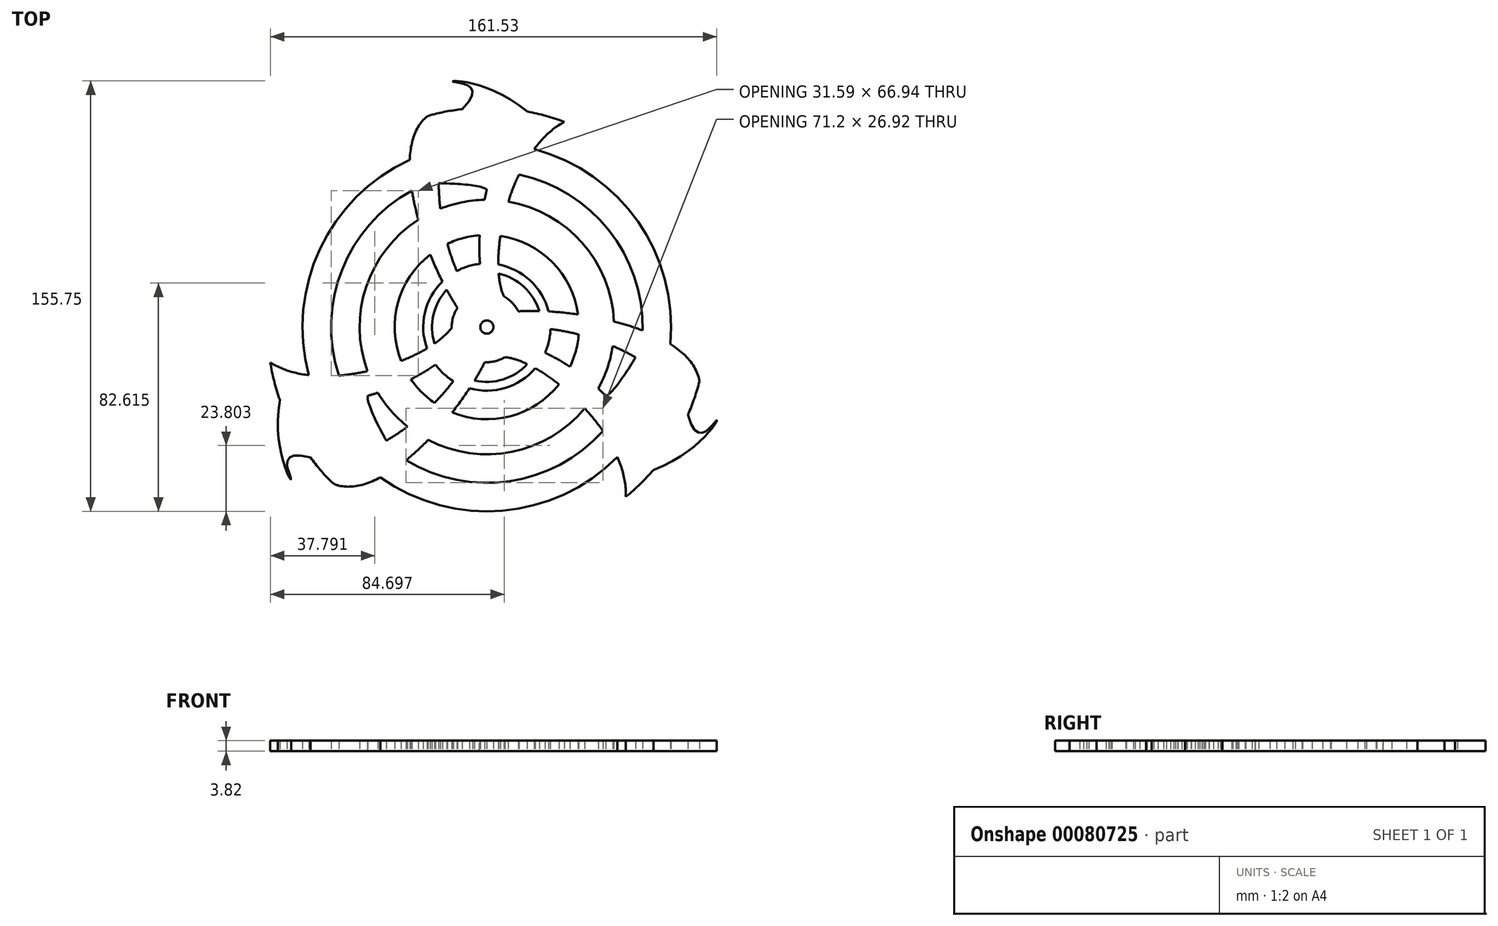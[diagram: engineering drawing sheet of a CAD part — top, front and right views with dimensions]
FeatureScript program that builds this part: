
annotation { "Feature Type Name" : "Feature", "Feature Type Description" : "" }
export const myFeature = defineFeature(function(context is Context, id is Id, definition is map)
    precondition{}
    {
        {
            var Q0;
            Q0=qCreatedBy(makeId("Top.planeOp"),FACE);
            var sketch = newSketch(context, id + "F0", { "sketchPlane" : qUnion([Q0])});
            skCircle(sketch, "E0", {"center": v(0, 0) * mm, "radius": 79.38 * mm});
            skCircle(sketch, "E1", {"center": v(0, 0) * mm, "radius": 2.37 * mm});
            skCircle(sketch, "E2", {"center": v(0, 0) * mm, "radius": 12.7 * mm});
            skFitSpline(sketch, "E3", {"points": [v(-10.61, 6.98) * mm, v(-21.43, 76.43) * mm], "startDerivative": vector(-34.7, 51.98) * mm, "endDerivative": vector(45.12, 35.8) * mm});
            skFitSpline(sketch, "E4", {"points": [v(6.15, 11.11) * mm, v(28.07, 74.25) * mm], "startDerivative": vector(-18.45, 41.17) * mm, "endDerivative": vector(59.8, 31.12) * mm});
            skFitSpline(sketch, "E5", {"points": [v(14.62, 78.02) * mm, v(-11.71, 88.69) * mm, v(-8.97, 78.87) * mm], "startDerivative": vector(-70.16, 57.99) * mm, "endDerivative": vector(-71.85, -70.05) * mm});
            skCircle(sketch, "E6", {"center": v(0, 0) * mm, "radius": 66.67 * mm});
            skFitSpline(sketch, "E7", {"points": [v(-5.9, 11.24) * mm, v(-8.97, 78.87) * mm], "startDerivative": vector(-30.89, 42.81) * mm, "endDerivative": vector(45.38, 50.1) * mm});
            skFitSpline(sketch, "E8", {"points": [v(0, 12.7) * mm, v(15.87, 77.77) * mm], "startDerivative": vector(-21.21, 46.5) * mm, "endDerivative": vector(47.62, 33.3) * mm});
            skCircle(sketch, "E9", {"center": v(0, 0) * mm, "radius": 46.04 * mm});
            skCircle(sketch, "E10", {"center": v(0, 0) * mm, "radius": 33.34 * mm});
            skLineSegment(sketch, "E11", {"start": v(-66.67, 0) * mm, "end": v(-46.04, 0) * mm, "construction": true});
            skLineSegment(sketch, "E12", {"start": v(-33.34, 0) * mm, "end": v(-12.7, 0) * mm, "construction": true});
            skLineSegment(sketch, "E13", {"start": v(33.34, 0) * mm, "end": v(46.04, 0) * mm, "construction": true});
            skLineSegment(sketch, "E14", {"start": v(66.67, 0) * mm, "end": v(79.38, 0) * mm, "construction": true});
            skCircle(sketch, "E15", {"center": v(0, 0) * mm, "radius": 56.36 * mm});
            skLineSegment(sketch, "E16", {"start": v(46.04, 0) * mm, "end": v(56.36, 0) * mm, "construction": true});
            skLineSegment(sketch, "E17", {"start": v(56.36, 0) * mm, "end": v(66.67, 0) * mm, "construction": true});
            skFitSpline(sketch, "E18", {"points": [v(0, 49.69) * mm, v(-22.08, 51.85) * mm], "startDerivative": vector(-3.5, 5.56) * mm, "endDerivative": vector(-20.7, -1.7) * mm});
            skCircle(sketch, "E19", {"center": v(0, 0) * mm, "radius": 23.02 * mm});
            skLineSegment(sketch, "E20", {"start": v(12.7, 0) * mm, "end": v(23.02, 0) * mm, "construction": true});
            skLineSegment(sketch, "E21", {"start": v(23.02, 0) * mm, "end": v(33.34, 0) * mm, "construction": true});
            skFitSpline(sketch, "E22", {"points": [v(-1.87, 18.8) * mm, v(-14.19, 18.13) * mm], "startDerivative": vector(-5.42, 2.86) * mm, "endDerivative": vector(-17.92, -7.29) * mm});
            skCircle(sketch, "E23", {"center": v(0, 0) * mm, "radius": 19.83 * mm});
            skSolve(sketch);
        }
        {
            var Q0;
            {var subQ0=sQuery(id+"F0.wireOp",EDGE,"E3");Q0=makeQuery(id+"F0.imprint","IMPRINT",FACE,{"disambiguationData":[TD([[makeQuery(id+"F0.imprint","IMPRINT",EDGE,{"derivedFrom":subQ0}),-1.0]])]});}
            var Q1;
            Q1=makeQuery(id+"F0.imprint","IMPRINT",FACE,{"disambiguationData":[TD([[makeQuery(id+"F0.imprint","IMPRINT",EDGE,{"derivedFrom":sQuery(id+"F0.wireOp",EDGE,"E1")}),-1.0]])]});
            var Q2;
            {var subQ0=sQuery(id+"F0.wireOp",EDGE,"E5");Q2=makeQuery(id+"F0.imprint","IMPRINT",FACE,{"disambiguationData":[TD([[makeQuery(id+"F0.imprint","IMPRINT",EDGE,{"derivedFrom":subQ0}),1.0]])]});}
            var Q3;
            {var subQ1=sQuery(id+"F0.wireOp",EDGE,"E5");var subQ2=sQuery(id+"F0.wireOp",EDGE,"E0");var subQ6=makeQuery(id+"F0.imprint","INTERSECT",VERTEX,{"derivedFrom":[subQ2,subQ1]});Q3=makeQuery(id+"F0.imprint","IMPRINT",FACE,{"disambiguationData":[TD([[makeQuery(id+"F0.imprint","IMPRINT",EDGE,{"disambiguationData":[TD([[subQ6,1.0]])],"derivedFrom":subQ2}),1.0]])]});}
            var Q4;
            {var subQ0=sQuery(id+"F0.wireOp",EDGE,"E4");var subQ1=sQuery(id+"F0.wireOp",EDGE,"E0");var subQ2=makeQuery(id+"F0.imprint","INTERSECT",VERTEX,{"derivedFrom":[subQ1,subQ0]});Q4=makeQuery(id+"F0.imprint","IMPRINT",FACE,{"disambiguationData":[TD([[makeQuery(id+"F0.imprint","IMPRINT",EDGE,{"disambiguationData":[TD([[subQ2,-1.0]])],"derivedFrom":subQ1}),1.0]])]});}
            var Q5;
            {var subQ0=sQuery(id+"F0.wireOp",EDGE,"E9");var subQ1=sQuery(id+"F0.wireOp",EDGE,"E4");var subQ2=makeQuery(id+"F0.imprint","INTERSECT",VERTEX,{"derivedFrom":[subQ1,subQ0]});Q5=makeQuery(id+"F0.imprint","IMPRINT",FACE,{"disambiguationData":[TD([[makeQuery(id+"F0.imprint","IMPRINT",EDGE,{"disambiguationData":[TD([[subQ2,-1.0]])],"derivedFrom":subQ1}),1.0]])]});}
            var Q6;
            {var subQ0=sQuery(id+"F0.wireOp",EDGE,"E10");var subQ1=sQuery(id+"F0.wireOp",EDGE,"E4");var subQ2=makeQuery(id+"F0.imprint","INTERSECT",VERTEX,{"derivedFrom":[subQ1,subQ0]});Q6=makeQuery(id+"F0.imprint","IMPRINT",FACE,{"disambiguationData":[TD([[makeQuery(id+"F0.imprint","IMPRINT",EDGE,{"disambiguationData":[TD([[subQ2,-1.0]])],"derivedFrom":subQ1}),1.0]])]});}
            var Q7;
            {var subQ0=sQuery(id+"F0.wireOp",EDGE,"E8");var subQ1=sQuery(id+"F0.wireOp",EDGE,"E2");var subQ2=makeQuery(id+"F0.imprint","INTERSECT",VERTEX,{"derivedFrom":[subQ1,subQ0]});Q7=makeQuery(id+"F0.imprint","IMPRINT",FACE,{"disambiguationData":[TD([[makeQuery(id+"F0.imprint","IMPRINT",EDGE,{"disambiguationData":[TD([[subQ2,1.0]])],"derivedFrom":subQ1}),-1.0]])]});}
            var Q8;
            {var subQ0=sQuery(id+"F0.wireOp",EDGE,"E10");var subQ1=sQuery(id+"F0.wireOp",EDGE,"E7");var subQ2=makeQuery(id+"F0.imprint","INTERSECT",VERTEX,{"derivedFrom":[subQ1,subQ0]});Q8=makeQuery(id+"F0.imprint","IMPRINT",FACE,{"disambiguationData":[TD([[makeQuery(id+"F0.imprint","IMPRINT",EDGE,{"disambiguationData":[TD([[subQ2,-1.0]])],"derivedFrom":subQ1}),-1.0]])]});}
            var Q9;
            {var subQ0=sQuery(id+"F0.wireOp",EDGE,"E9");var subQ1=sQuery(id+"F0.wireOp",EDGE,"E3");var subQ2=makeQuery(id+"F0.imprint","INTERSECT",VERTEX,{"derivedFrom":[subQ1,subQ0]});Q9=makeQuery(id+"F0.imprint","IMPRINT",FACE,{"disambiguationData":[TD([[makeQuery(id+"F0.imprint","IMPRINT",EDGE,{"disambiguationData":[TD([[subQ2,-1.0]])],"derivedFrom":subQ1}),-1.0]])]});}
            var Q10;
            {var subQ0=sQuery(id+"F0.wireOp",EDGE,"02ee5eb9-fec3-4d49-90e1-4be1db1b977d");Q10=makeQuery(id+"F0.imprint","IMPRINT",FACE,{"disambiguationData":[TD([[makeQuery(id+"F0.imprint","IMPRINT",EDGE,{"derivedFrom":subQ0}),1.0]])]});}
            var Q11;
            {var subQ0=sQuery(id+"F0.wireOp",EDGE,"E15");var subQ1=sQuery(id+"F0.wireOp",EDGE,"E4");var subQ2=makeQuery(id+"F0.imprint","INTERSECT",VERTEX,{"derivedFrom":[subQ1,subQ0]});Q11=makeQuery(id+"F0.imprint","IMPRINT",FACE,{"disambiguationData":[TD([[makeQuery(id+"F0.imprint","IMPRINT",EDGE,{"disambiguationData":[TD([[subQ2,-1.0]])],"derivedFrom":subQ1}),1.0]])]});}
            var Q12;
            {var subQ0=sQuery(id+"F0.wireOp",EDGE,"E18");Q12=makeQuery(id+"F0.imprint","IMPRINT",FACE,{"disambiguationData":[TD([[makeQuery(id+"F0.imprint","IMPRINT",EDGE,{"derivedFrom":subQ0}),-1.0]])]});}
            var Q13;
            {var subQ4=sQuery(id+"F0.wireOp",EDGE,"E2");var subQ6=sQuery(id+"F0.wireOp",EDGE,"E3");var subQ7=makeQuery(id+"F0.imprint","INTERSECT",VERTEX,{"derivedFrom":[subQ4,subQ6]});Q13=makeQuery(id+"F0.imprint","IMPRINT",FACE,{"disambiguationData":[TD([[makeQuery(id+"F0.imprint","IMPRINT",EDGE,{"disambiguationData":[TD([[subQ7,1.0]])],"derivedFrom":subQ4}),-1.0]])]});}
            var Q14;
            {var subQ0=sQuery(id+"F0.wireOp",EDGE,"b8c473f6-a033-4eba-b6a9-50cacf2a13a1");Q14=makeQuery(id+"F0.imprint","IMPRINT",FACE,{"disambiguationData":[TD([[makeQuery(id+"F0.imprint","IMPRINT",EDGE,{"derivedFrom":subQ0}),1.0]])]});}
            var Q15;
            {var subQ0=sQuery(id+"F0.wireOp",EDGE,"E19");var subQ1=sQuery(id+"F0.wireOp",EDGE,"E4");var subQ2=makeQuery(id+"F0.imprint","INTERSECT",VERTEX,{"derivedFrom":[subQ1,subQ0]});Q15=makeQuery(id+"F0.imprint","IMPRINT",FACE,{"disambiguationData":[TD([[makeQuery(id+"F0.imprint","IMPRINT",EDGE,{"disambiguationData":[TD([[subQ2,-1.0]])],"derivedFrom":subQ1}),1.0]])]});}
            var Q16;
            {var subQ0=sQuery(id+"F0.wireOp",EDGE,"E22");Q16=makeQuery(id+"F0.imprint","IMPRINT",FACE,{"disambiguationData":[TD([[makeQuery(id+"F0.imprint","IMPRINT",EDGE,{"derivedFrom":subQ0}),-1.0]])]});}
            var Q17;
            {var subQ1=sQuery(id+"F0.wireOp",EDGE,"E3");var subQ5=sQuery(id+"F0.wireOp",EDGE,"E19");var subQ8=makeQuery(id+"F0.imprint","INTERSECT",VERTEX,{"derivedFrom":[subQ1,subQ5]});Q17=makeQuery(id+"F0.imprint","IMPRINT",FACE,{"disambiguationData":[TD([[makeQuery(id+"F0.imprint","IMPRINT",EDGE,{"disambiguationData":[TD([[subQ8,-1.0]])],"derivedFrom":subQ1}),-1.0]])]});}
            var Q18;
            {var subQ0=sQuery(id+"F0.wireOp",EDGE,"E22");var subQ1=sQuery(id+"F0.wireOp",EDGE,"E7");var subQ2=makeQuery(id+"F0.imprint","INTERSECT",VERTEX,{"derivedFrom":[subQ1,subQ0]});Q18=makeQuery(id+"F0.imprint","IMPRINT",FACE,{"disambiguationData":[TD([[makeQuery(id+"F0.imprint","IMPRINT",EDGE,{"disambiguationData":[TD([[subQ2,-1.0]])],"derivedFrom":subQ1}),-1.0]])]});}
            var Q19;
            {var subQ0=sQuery(id+"F0.wireOp",EDGE,"E7");var subQ1=sQuery(id+"F0.wireOp",EDGE,"E2");var subQ2=makeQuery(id+"F0.imprint","INTERSECT",VERTEX,{"derivedFrom":[subQ1,subQ0]});Q19=makeQuery(id+"F0.imprint","IMPRINT",FACE,{"disambiguationData":[TD([[makeQuery(id+"F0.imprint","IMPRINT",EDGE,{"disambiguationData":[TD([[subQ2,1.0]])],"derivedFrom":subQ1}),-1.0]])]});}
            var Q20;
            {var subQ0=sQuery(id+"F0.wireOp",EDGE,"E23");var subQ1=sQuery(id+"F0.wireOp",EDGE,"E4");var subQ2=makeQuery(id+"F0.imprint","INTERSECT",VERTEX,{"derivedFrom":[subQ1,subQ0]});Q20=makeQuery(id+"F0.imprint","IMPRINT",FACE,{"disambiguationData":[TD([[makeQuery(id+"F0.imprint","IMPRINT",EDGE,{"disambiguationData":[TD([[subQ2,-1.0]])],"derivedFrom":subQ1}),1.0]])]});}
            var Q21;
            {var subQ5=sQuery(id+"F0.wireOp",EDGE,"E3");var subQ7=sQuery(id+"F0.wireOp",EDGE,"E23");var subQ9=makeQuery(id+"F0.imprint","INTERSECT",VERTEX,{"derivedFrom":[subQ5,subQ7]});Q21=makeQuery(id+"F0.imprint","IMPRINT",FACE,{"disambiguationData":[TD([[makeQuery(id+"F0.imprint","IMPRINT",EDGE,{"disambiguationData":[TD([[subQ9,-1.0]])],"derivedFrom":subQ5}),-1.0]])]});}
            var Q22;
            {var subQ0=sQuery(id+"F0.wireOp",EDGE,"E23");var subQ1=sQuery(id+"F0.wireOp",EDGE,"E3");var subQ2=makeQuery(id+"F0.imprint","INTERSECT",VERTEX,{"derivedFrom":[subQ1,subQ0]});Q22=makeQuery(id+"F0.imprint","IMPRINT",FACE,{"disambiguationData":[TD([[makeQuery(id+"F0.imprint","IMPRINT",EDGE,{"disambiguationData":[TD([[subQ2,-1.0]])],"derivedFrom":subQ1}),1.0]])]});}
            var Q23;
            {var subQ0=sQuery(id+"F0.wireOp",EDGE,"E10");var subQ1=sQuery(id+"F0.wireOp",EDGE,"E3");var subQ2=makeQuery(id+"F0.imprint","INTERSECT",VERTEX,{"derivedFrom":[subQ1,subQ0]});Q23=makeQuery(id+"F0.imprint","IMPRINT",FACE,{"disambiguationData":[TD([[makeQuery(id+"F0.imprint","IMPRINT",EDGE,{"disambiguationData":[TD([[subQ2,-1.0]])],"derivedFrom":subQ1}),1.0]])]});}
            var Q24;
            {var subQ3=sQuery(id+"F0.wireOp",EDGE,"E15");var subQ6=sQuery(id+"F0.wireOp",EDGE,"E3");var subQ8=makeQuery(id+"F0.imprint","INTERSECT",VERTEX,{"derivedFrom":[subQ6,subQ3]});Q24=makeQuery(id+"F0.imprint","IMPRINT",FACE,{"disambiguationData":[TD([[makeQuery(id+"F0.imprint","IMPRINT",EDGE,{"disambiguationData":[TD([[subQ8,-1.0]])],"derivedFrom":subQ6}),-1.0]])]});}
            var Q25;
            {var subQ0=sQuery(id+"F0.wireOp",EDGE,"E18");var subQ1=sQuery(id+"F0.wireOp",EDGE,"E7");var subQ2=makeQuery(id+"F0.imprint","INTERSECT",VERTEX,{"derivedFrom":[subQ1,subQ0]});Q25=makeQuery(id+"F0.imprint","IMPRINT",FACE,{"disambiguationData":[TD([[makeQuery(id+"F0.imprint","IMPRINT",EDGE,{"disambiguationData":[TD([[subQ2,-1.0]])],"derivedFrom":subQ1}),-1.0]])]});}
            var Q26;
            {var subQ0=sQuery(id+"F0.wireOp",EDGE,"E15");var subQ1=sQuery(id+"F0.wireOp",EDGE,"E3");var subQ2=makeQuery(id+"F0.imprint","INTERSECT",VERTEX,{"derivedFrom":[subQ1,subQ0]});Q26=makeQuery(id+"F0.imprint","IMPRINT",FACE,{"disambiguationData":[TD([[makeQuery(id+"F0.imprint","IMPRINT",EDGE,{"disambiguationData":[TD([[subQ2,-1.0]])],"derivedFrom":subQ1}),1.0]])]});}
            extrude(context, id + "F1", {"entities" : qUnion([Q0, Q1, Q2, Q3, Q4, Q5, Q6, Q7, Q8, Q9, Q10, Q11, Q12, Q13, Q14, Q15, Q16, Q17, Q18, Q19, Q20, Q21, Q22, Q23, Q24, Q25, Q26]), "endBound" : BoundingType.SYMMETRIC, "depth" : 3.8 * mm});
        }
        {
            var Q0;
            Q0=makeQuery(id+"F1.opExtrude","SWEPT_BODY",BODY,{"disambiguationData":[OSD([sQuery(id+"F0.wireOp",EDGE,"E0"),sQuery(id+"F0.wireOp",EDGE,"E1"),sQuery(id+"F0.wireOp",EDGE,"E2"),sQuery(id+"F0.wireOp",EDGE,"E3"),sQuery(id+"F0.wireOp",EDGE,"E4"),sQuery(id+"F0.wireOp",EDGE,"E5")])]});
            var Q1;
            Q1=makeQuery(id+"F1.opExtrude","CAP_EDGE",EDGE,{"disambiguationData":[OSD([sQuery(id+"F0.wireOp",EDGE,"E1")])],"isStart":false});
            circularPattern(context, id + "F2", {"operationType" : NewBodyOperationType.ADD, "entities" : qUnion([Q0]), "axis" : qUnion([Q1]), "angle" : 360 * degree, "instanceCount" : 3, "equalSpace" : true});
        }
        {
            var Q0;
            Q0=makeQuery(id+"F1.opExtrude","SWEPT_EDGE",EDGE,{"disambiguationData":[OSD([sQuery(id+"F0.wireOp",EDGE,"E0"),sQuery(id+"F0.wireOp",EDGE,"E3")])]});
            var Q1;
            Q1=makeQuery(id+"F2.opPattern","COPY",EDGE,{"derivedFrom":makeQuery(id+"F1.opExtrude","SWEPT_EDGE",EDGE,{"disambiguationData":[OSD([sQuery(id+"F0.wireOp",EDGE,"E0"),sQuery(id+"F0.wireOp",EDGE,"E3")])]}),"instanceName":"1"});
            fillet(context, id + "F3", {"entities" : qUnion([Q0, Q1]), "radius" : 5.08 * mm, "tangentPropagation" : true, "allowEdgeOverflow" : false});
        }
    });
